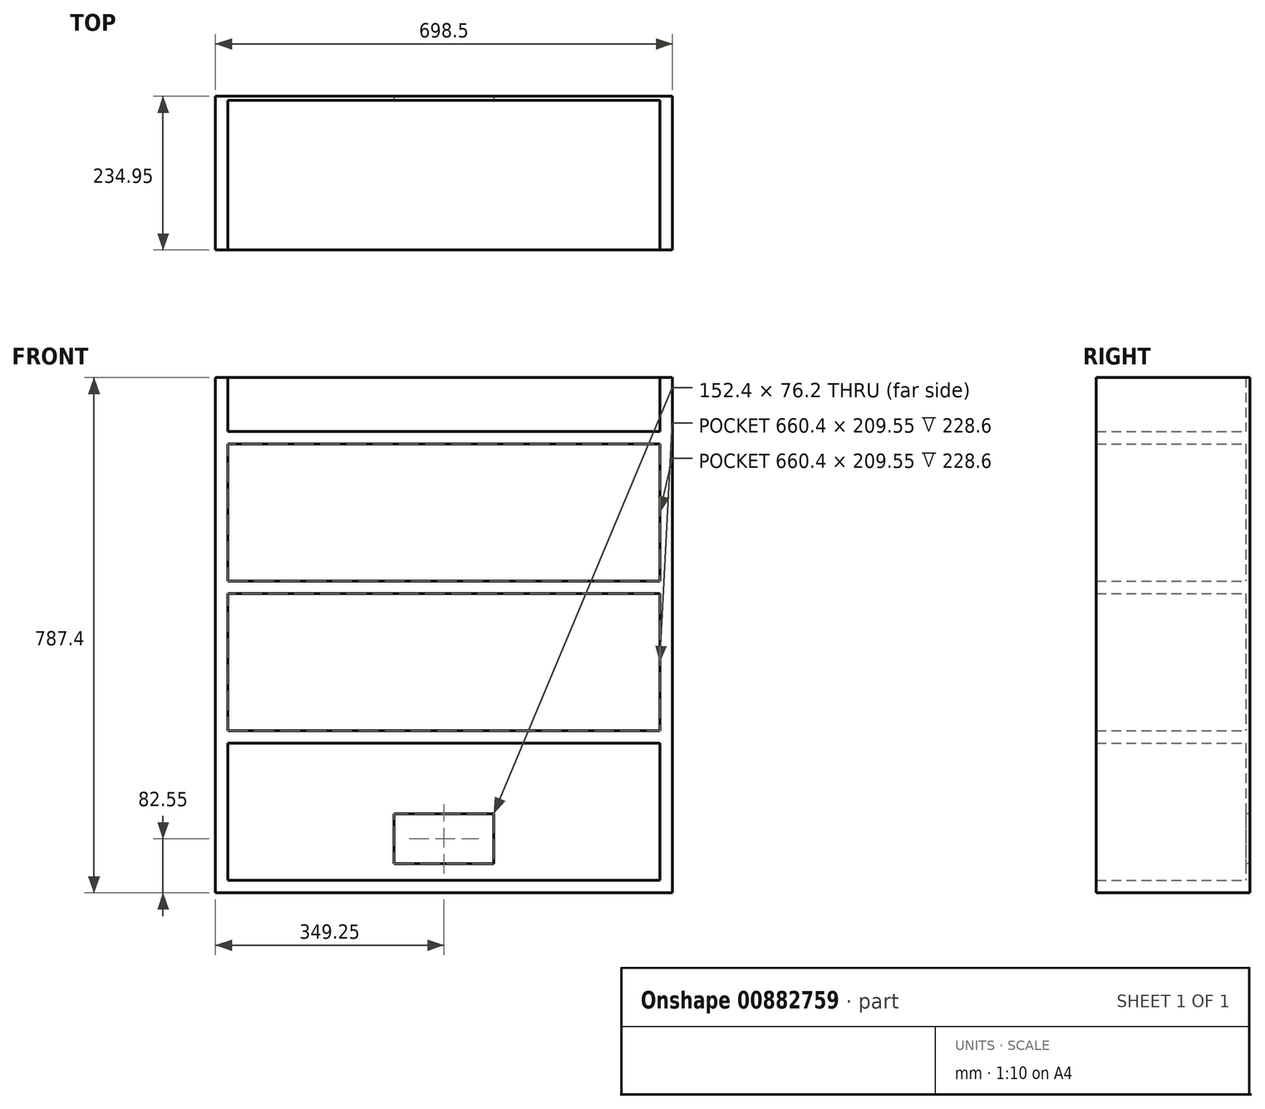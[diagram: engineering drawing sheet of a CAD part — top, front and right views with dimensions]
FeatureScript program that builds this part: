
annotation { "Feature Type Name" : "Feature", "Feature Type Description" : "" }
export const myFeature = defineFeature(function(context is Context, id is Id, definition is map)
    precondition{}
    {
        {
            var Q0;
            Q0=qCreatedBy(makeId("Front.planeOp"),FACE);
            var sketch = newSketch(context, id + "F0", { "sketchPlane" : qUnion([Q0])});
            skLineSegment(sketch, "E0.bottom", {"start": v(0, 0) * mm, "end": v(698.5, 0) * mm});
            skLineSegment(sketch, "E0.top", {"start": v(0, 787.4) * mm, "end": v(698.5, 787.4) * mm});
            skLineSegment(sketch, "E0.left", {"start": v(0, 0) * mm, "end": v(0, 787.4) * mm});
            skLineSegment(sketch, "E0.right", {"start": v(698.5, 0) * mm, "end": v(698.5, 787.4) * mm});
            skSolve(sketch);
        }
        {
            var Q0;
            Q0=makeQuery(id+"F0.imprint","IMPRINT",FACE,{"disambiguationData":[TD([[makeQuery(id+"F0.imprint","IMPRINT",EDGE,{"derivedFrom":sQuery(id+"F0.wireOp",EDGE,"E0.bottom")}),1.0]])]});
            extrude(context, id + "F1", {"entities" : qUnion([Q0]), "depth" : 6.35 * mm, "offsetDistance" : 25.4 * mm});
        }
        {
            var Q0;
            Q0=makeQuery(id+"F1.opExtrude","CAP_FACE",FACE,{"disambiguationData":[OSD([sQuery(id+"F0.wireOp",EDGE,"E0.bottom"),sQuery(id+"F0.wireOp",EDGE,"E0.top"),sQuery(id+"F0.wireOp",EDGE,"E0.left"),sQuery(id+"F0.wireOp",EDGE,"E0.right")])],"isStart":false});
            var sketch = newSketch(context, id + "F2", { "sketchPlane" : qUnion([Q0])});
            skLineSegment(sketch, "E1.bottom", {"start": v(0, 787.4) * mm, "end": v(19.05, 787.4) * mm});
            skLineSegment(sketch, "E1.top", {"start": v(0, 0) * mm, "end": v(19.05, 0) * mm});
            skLineSegment(sketch, "E1.left", {"start": v(0, 787.4) * mm, "end": v(0, 0) * mm});
            skLineSegment(sketch, "E1.right", {"start": v(19.05, 787.4) * mm, "end": v(19.05, 0) * mm});
            skLineSegment(sketch, "E2.bottom", {"start": v(698.5, 787.4) * mm, "end": v(679.45, 787.4) * mm});
            skLineSegment(sketch, "E2.top", {"start": v(698.5, 0) * mm, "end": v(679.45, 0) * mm});
            skLineSegment(sketch, "E2.left", {"start": v(698.5, 787.4) * mm, "end": v(698.5, 0) * mm});
            skLineSegment(sketch, "E2.right", {"start": v(679.45, 787.4) * mm, "end": v(679.45, 0) * mm});
            skLineSegment(sketch, "E3.bottom", {"start": v(19.05, 19.05) * mm, "end": v(679.45, 19.05) * mm});
            skLineSegment(sketch, "E3.top", {"start": v(19.05, 0) * mm, "end": v(679.45, 0) * mm});
            skLineSegment(sketch, "E3.left", {"start": v(19.05, 19.05) * mm, "end": v(19.05, 0) * mm});
            skLineSegment(sketch, "E3.right", {"start": v(679.45, 19.05) * mm, "end": v(679.45, 0) * mm});
            skLineSegment(sketch, "E4.bottom", {"start": v(19.05, 228.6) * mm, "end": v(679.45, 228.6) * mm});
            skLineSegment(sketch, "E4.top", {"start": v(19.05, 247.65) * mm, "end": v(679.45, 247.65) * mm});
            skLineSegment(sketch, "E4.left", {"start": v(19.05, 247.65) * mm, "end": v(19.05, 228.6) * mm});
            skLineSegment(sketch, "E4.right", {"start": v(679.45, 247.65) * mm, "end": v(679.45, 228.6) * mm});
            skLineSegment(sketch, "E5.top", {"start": v(19.05, 457.2) * mm, "end": v(679.45, 457.2) * mm});
            skLineSegment(sketch, "E6", {"start": v(19.05, 476.25) * mm, "end": v(679.45, 476.25) * mm});
            skLineSegment(sketch, "E7", {"start": v(679.45, 685.8) * mm, "end": v(19.05, 685.8) * mm});
            skLineSegment(sketch, "E8", {"start": v(19.05, 685.8) * mm, "end": v(19.05, 704.85) * mm});
            skLineSegment(sketch, "E9", {"start": v(19.05, 704.85) * mm, "end": v(679.45, 704.85) * mm});
            skSolve(sketch);
        }
        {
            var Q0;
            {var subQ6=sQuery(id+"F2.wireOp",EDGE,"E1.bottom");Q0=makeQuery(id+"F2.imprint","IMPRINT",FACE,{"disambiguationData":[TD([[makeQuery(id+"F2.imprint","IMPRINT",EDGE,{"derivedFrom":subQ6}),-1.0]])]});}
            var Q1;
            {var subQ7=sQuery(id+"F2.wireOp",EDGE,"E2.bottom");Q1=makeQuery(id+"F2.imprint","IMPRINT",FACE,{"disambiguationData":[TD([[makeQuery(id+"F2.imprint","IMPRINT",EDGE,{"derivedFrom":subQ7}),-1.0]])]});}
            var Q2;
            {var subQ0=sQuery(id+"F2.wireOp",EDGE,"E7");Q2=makeQuery(id+"F2.imprint","IMPRINT",FACE,{"disambiguationData":[TD([[makeQuery(id+"F2.imprint","IMPRINT",EDGE,{"derivedFrom":subQ0}),-1.0]])]});}
            var Q3;
            {var subQ0=sQuery(id+"F2.wireOp",EDGE,"E5.top");Q3=makeQuery(id+"F2.imprint","IMPRINT",FACE,{"disambiguationData":[TD([[makeQuery(id+"F2.imprint","IMPRINT",EDGE,{"derivedFrom":subQ0}),1.0]])]});}
            var Q4;
            Q4=makeQuery(id+"F2.imprint","IMPRINT",FACE,{"disambiguationData":[TD([[makeQuery(id+"F2.imprint","IMPRINT",EDGE,{"derivedFrom":sQuery(id+"F2.wireOp",EDGE,"E4.bottom")}),1.0]])]});
            var Q5;
            Q5=makeQuery(id+"F2.imprint","IMPRINT",FACE,{"disambiguationData":[TD([[makeQuery(id+"F2.imprint","IMPRINT",EDGE,{"derivedFrom":sQuery(id+"F2.wireOp",EDGE,"E3.bottom")}),-1.0]])]});
            extrude(context, id + "F3", {"entities" : qUnion([Q0, Q1, Q2, Q3, Q4, Q5]), "operationType" : NewBodyOperationType.ADD, "depth" : 228.6 * mm, "offsetDistance" : 25.4 * mm});
        }
        {
            var Q0;
            {var subQ0=sQuery(id+"F2.wireOp",EDGE,"E3.bottom");Q0=makeQuery(id+"F3.boolean.opBoolean","SPLIT",FACE,{"disambiguationData":[TD([makeQuery(id+"F3.opExtrude","SWEPT_FACE",FACE,{"disambiguationData":[OSD([subQ0])]})])],"derivedFrom":makeQuery(id+"F1.opExtrude","CAP_FACE",FACE,{"disambiguationData":[OSD([sQuery(id+"F0.wireOp",EDGE,"E0.bottom"),sQuery(id+"F0.wireOp",EDGE,"E0.top"),sQuery(id+"F0.wireOp",EDGE,"E0.left"),sQuery(id+"F0.wireOp",EDGE,"E0.right")])],"isStart":false})});}
            var sketch = newSketch(context, id + "F4", { "sketchPlane" : qUnion([Q0])});
            skLineSegment(sketch, "E10.bottom", {"start": v(273.05, 806.45) * mm, "end": v(425.45, 806.45) * mm});
            skLineSegment(sketch, "E10.top", {"start": v(273.05, 730.25) * mm, "end": v(425.45, 730.25) * mm});
            skLineSegment(sketch, "E10.left", {"start": v(273.05, 806.45) * mm, "end": v(273.05, 730.25) * mm});
            skLineSegment(sketch, "E10.right", {"start": v(425.45, 806.45) * mm, "end": v(425.45, 730.25) * mm});
            skLineSegment(sketch, "E11.bottom", {"start": v(273.05, 120.65) * mm, "end": v(425.45, 120.65) * mm});
            skLineSegment(sketch, "E11.top", {"start": v(273.05, 44.45) * mm, "end": v(425.45, 44.45) * mm});
            skLineSegment(sketch, "E11.left", {"start": v(273.05, 120.65) * mm, "end": v(273.05, 44.45) * mm});
            skLineSegment(sketch, "E11.right", {"start": v(425.45, 120.65) * mm, "end": v(425.45, 44.45) * mm});
            skSolve(sketch);
        }
        {
            var Q0;
            Q0=makeQuery(id+"F4.imprint","IMPRINT",FACE,{"disambiguationData":[TD([[makeQuery(id+"F4.imprint","IMPRINT",EDGE,{"derivedFrom":sQuery(id+"F4.wireOp",EDGE,"E10.bottom")}),-1.0]])]});
            var Q1;
            Q1=makeQuery(id+"F4.imprint","IMPRINT",FACE,{"disambiguationData":[TD([[makeQuery(id+"F4.imprint","IMPRINT",EDGE,{"derivedFrom":sQuery(id+"F4.wireOp",EDGE,"E11.bottom")}),-1.0]])]});
            extrude(context, id + "F5", {"entities" : qUnion([Q0, Q1]), "operationType" : NewBodyOperationType.REMOVE, "oppositeDirection" : true, "depth" : 25.4 * mm, "offsetDistance" : 25.4 * mm});
        }
    });
